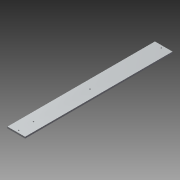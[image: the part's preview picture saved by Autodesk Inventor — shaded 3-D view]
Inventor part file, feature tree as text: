
AUTODESK INVENTOR PART (.ipt)
format: ipt  version: 2015 SP1 (Build 190203100, 203)  size: 95,232 bytes
history: native  units: mm
features: reference x4, sketch x2, extrude x1, hole x1
ambient origin geometry x8: Origin, YZ Plane, XZ Plane, XY Plane, X Axis, Y Axis, Z Axis, Center Point
bodies: Solid1 (feature_tree)
feature tree (8):
  extrude  "Extrusion1"  Depth=6.35mm
  hole  "Hole1"  [1 undecoded]
  sketch  "Sketch1"  dims[d0=6.35mm d1=0.0mm d2=20.0mm]
  reference  "Reference1"
  reference  "Reference2"
  reference  "Reference3"
  reference  "Reference4"
  sketch  "Sketch2"  dims[d3=140.0mm d4=20.0mm d5=4.5mm d6=6.0mm d7=8.0mm d8=4.0mm d9=90.0deg d10=8.0mm d11=20.594885mm]
note: 1 required parameter value undecoded (feature->parameter linkage not recoverable at this tier; creation-order binding heuristic only, values carry confidence <= 0.55)
